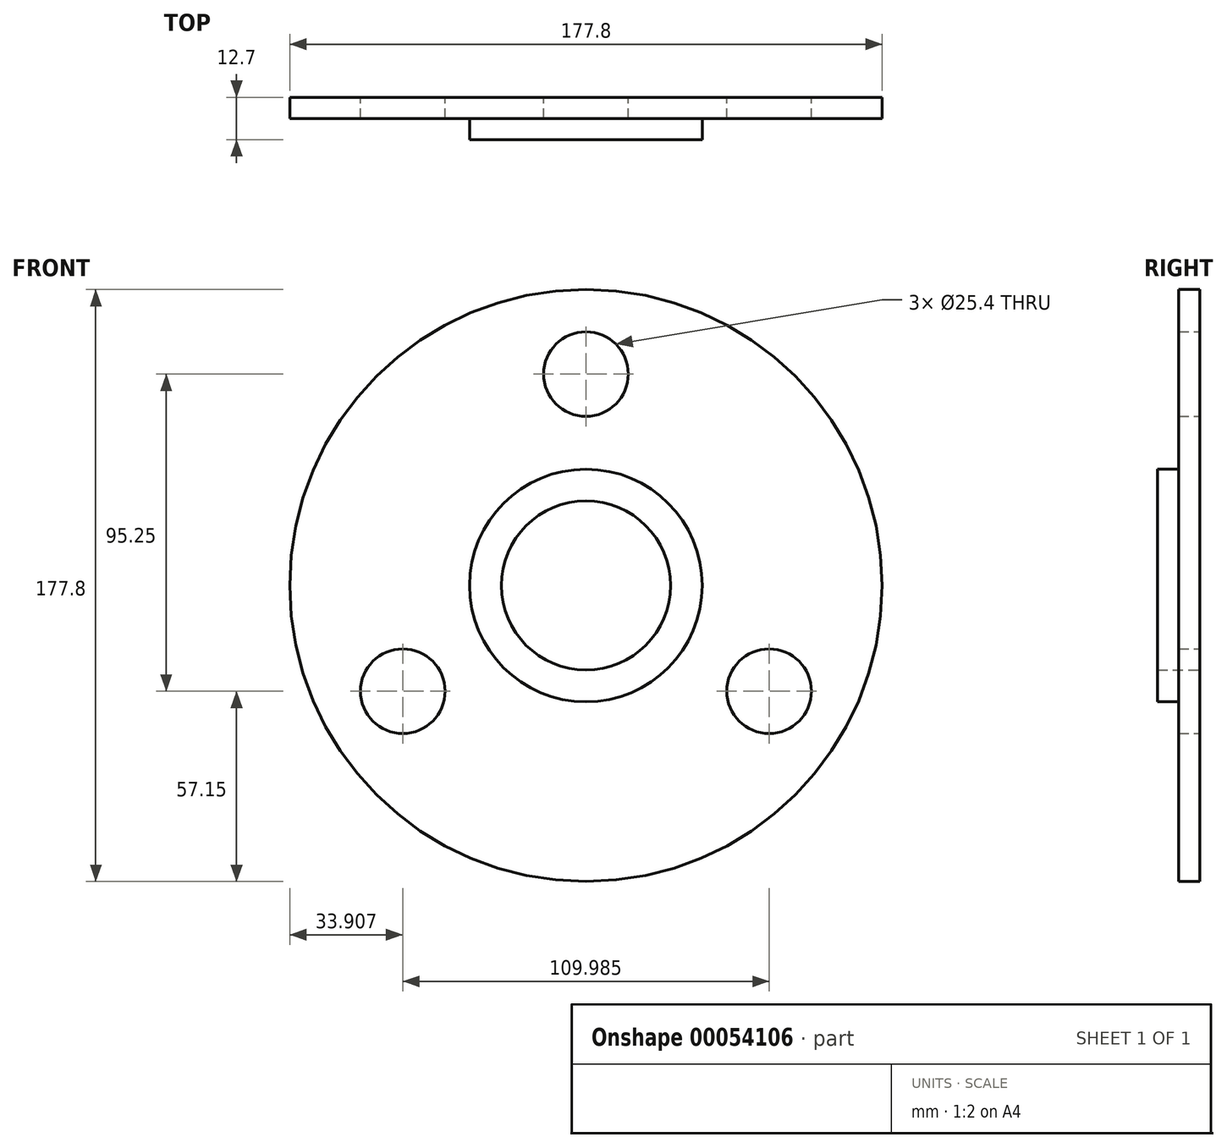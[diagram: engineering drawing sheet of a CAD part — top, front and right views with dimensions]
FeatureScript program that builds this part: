
annotation { "Feature Type Name" : "Feature", "Feature Type Description" : "" }
export const myFeature = defineFeature(function(context is Context, id is Id, definition is map)
    precondition{}
    {
        {
            var Q0;
            Q0=qCreatedBy(makeId("Front.planeOp"),FACE);
            var sketch = newSketch(context, id + "F0", { "sketchPlane" : qUnion([Q0])});
            skCircle(sketch, "E0", {"center": v(0, 0) * mm, "radius": 88.9 * mm});
            skCircle(sketch, "E1", {"center": v(0, 0) * mm, "radius": 25.4 * mm});
            skCircle(sketch, "E2", {"center": v(0, 0) * mm, "radius": 34.93 * mm});
            skCircle(sketch, "E3", {"center": v(0, 0) * mm, "radius": 63.5 * mm, "construction": true});
            skCircle(sketch, "E4", {"center": v(0, 63.5) * mm, "radius": 12.7 * mm});
            skCircle(sketch, "E5.1.0", {"center": v(-55, -31.75) * mm, "radius": 12.7 * mm});
            skCircle(sketch, "E5.2.0", {"center": v(55, -31.75) * mm, "radius": 12.7 * mm});
            skSolve(sketch);
        }
        {
            var Q0;
            Q0 = qSketchRegion(id + "F0", true);
            extrude(context, id + "F1", {"entities" : qUnion([Q0]), "depth" : 6.35 * mm});
        }
        {
            var Q0;
            Q0=makeQuery(id+"F0.imprint","IMPRINT",FACE,{"disambiguationData":[TD([[makeQuery(id+"F0.imprint","IMPRINT",EDGE,{"derivedFrom":sQuery(id+"F0.wireOp",EDGE,"E1")}),-1.0]])]});
            extrude(context, id + "F2", {"entities" : qUnion([Q0]), "operationType" : NewBodyOperationType.ADD, "depth" : 12.7 * mm});
        }
    });
